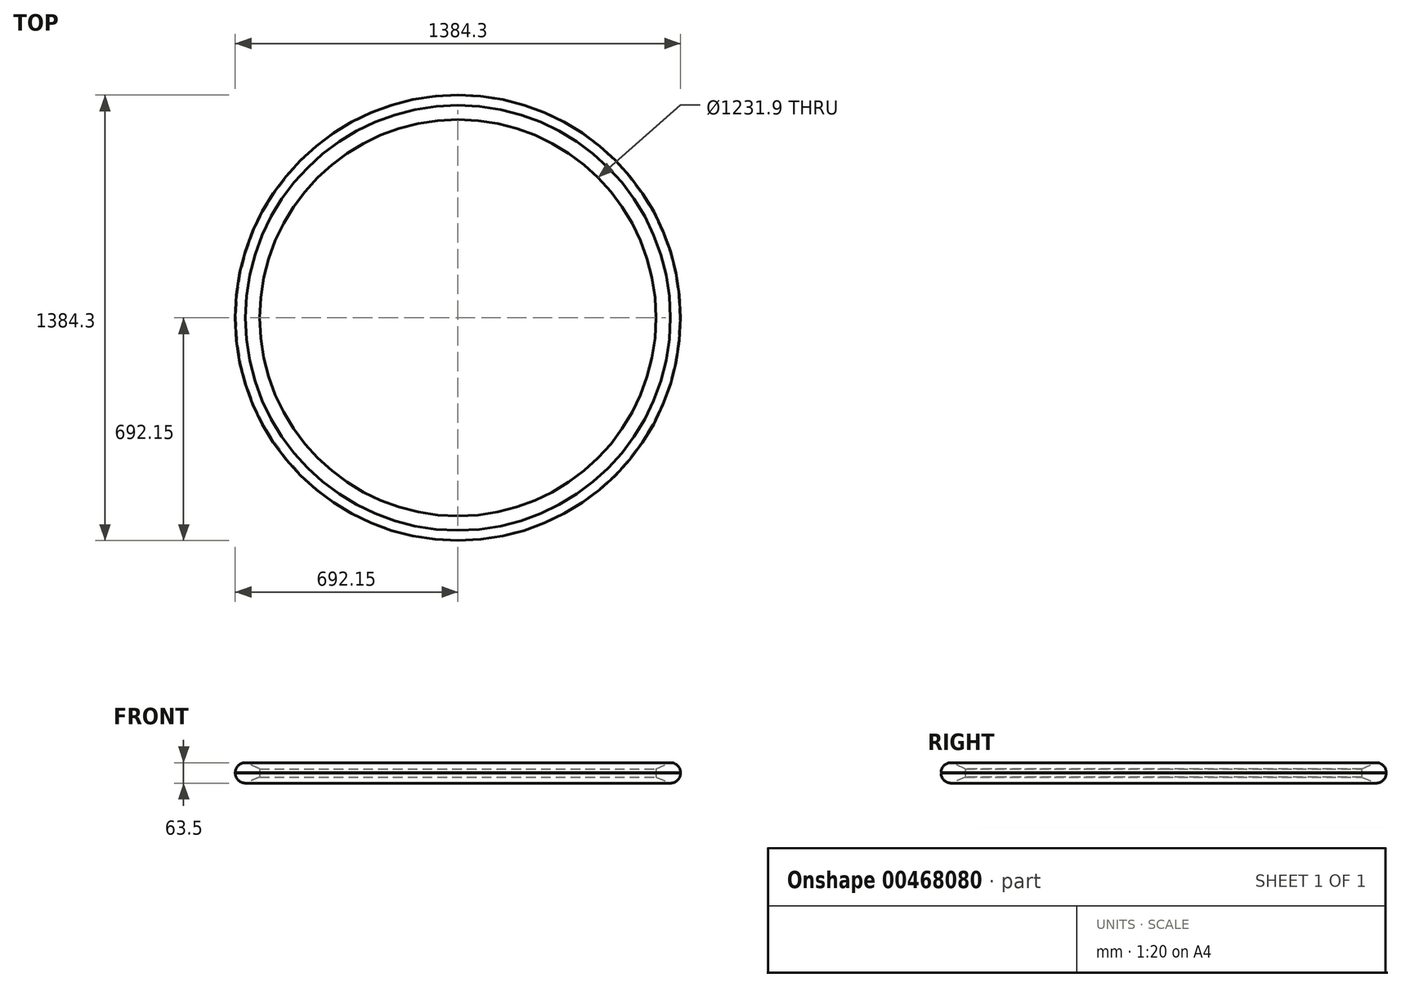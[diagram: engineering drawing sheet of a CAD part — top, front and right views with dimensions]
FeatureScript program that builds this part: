
annotation { "Feature Type Name" : "Feature", "Feature Type Description" : "" }
export const myFeature = defineFeature(function(context is Context, id is Id, definition is map)
    precondition{}
    {
        {
            var Q0;
            Q0=qCreatedBy(makeId("Front.planeOp"),FACE);
            var sketch = newSketch(context, id + "F0", { "sketchPlane" : qUnion([Q0])});
            skLineSegment(sketch, "E0", {"start": v(0, 0) * mm, "end": v(660.4, 0) * mm});
            skLineSegment(sketch, "E1", {"start": v(660.4, 0) * mm, "end": v(615.95, 0) * mm});
            skLineSegment(sketch, "E2", {"start": v(615.95, 0) * mm, "end": v(615.95, 12.7) * mm});
            skLineSegment(sketch, "E3", {"start": v(615.95, 0) * mm, "end": v(615.95, -12.7) * mm});
            skLineSegment(sketch, "E4", {"start": v(0, 0) * mm, "end": v(0, 83.21) * mm});
            skCircle(sketch, "E5", {"center": v(660.4, 0) * mm, "radius": 31.75 * mm});
            skLineSegment(sketch, "E6", {"start": v(615.95, -12.7) * mm, "end": v(660.4, -31.75) * mm});
            skLineSegment(sketch, "E7", {"start": v(615.95, 12.7) * mm, "end": v(660.4, 31.75) * mm});
            skLineSegment(sketch, "E8", {"start": v(692.15, 0) * mm, "end": v(689.6, 0) * mm});
            skLineSegment(sketch, "E9", {"start": v(689.6, 0) * mm, "end": v(689.6, 0.25) * mm});
            skLineSegment(sketch, "E10", {"start": v(689.6, 0.25) * mm, "end": v(692.15, 0.25) * mm});
            skLineSegment(sketch, "E11", {"start": v(689.6, 0) * mm, "end": v(689.6, -0.25) * mm});
            skLineSegment(sketch, "E12", {"start": v(689.6, -0.25) * mm, "end": v(692.15, -0.25) * mm});
            skSolve(sketch);
        }
        {
            var Q0;
            {var subQ0=sQuery(id+"F0.wireOp",EDGE,"BpbeHqKv-90v2-CecC-KdAu-xhUZU532047C");var subQ1=sQuery(id+"F0.wireOp",EDGE,"ouEWdRrN-fbvK-T4IV-dJUb-a4UaIsFi8zsm");var subQ2=makeQuery(id+"F0.imprint","INTERSECT",VERTEX,{"disambiguationData":[OD(0.0)],"derivedFrom":[subQ1,subQ0]});Q0=makeQuery(id+"F0.imprint","IMPRINT",FACE,{"disambiguationData":[TD([[makeQuery(id+"F0.imprint","IMPRINT",EDGE,{"disambiguationData":[TD([[subQ2,-1.0]])],"derivedFrom":subQ1}),1.0]])]});}
            var Q1;
            {var subQ0=sQuery(id+"F0.wireOp",EDGE,"BpbeHqKv-90v2-CecC-KdAu-xhUZU532047C");var subQ1=sQuery(id+"F0.wireOp",EDGE,"ouEWdRrN-fbvK-T4IV-dJUb-a4UaIsFi8zsm");var subQ3=makeQuery(id+"F0.imprint","INTERSECT",VERTEX,{"disambiguationData":[OD(1.0)],"derivedFrom":[subQ1,subQ0]});Q1=makeQuery(id+"F0.imprint","IMPRINT",FACE,{"disambiguationData":[TD([[makeQuery(id+"F0.imprint","IMPRINT",EDGE,{"disambiguationData":[TD([[subQ3,-1.0]])],"derivedFrom":subQ1}),1.0]])]});}
            var Q2;
            {var subQ0=sQuery(id+"F0.wireOp",EDGE,"VjwYH7CL-qhdJ-UY1F-Rfc4-S9BnykVlBEnN");var subQ1=sQuery(id+"F0.wireOp",EDGE,"ouEWdRrN-fbvK-T4IV-dJUb-a4UaIsFi8zsm");var subQ2=makeQuery(id+"F0.imprint","INTERSECT",VERTEX,{"disambiguationData":[OD(0.0)],"derivedFrom":[subQ1,subQ0]});Q2=makeQuery(id+"F0.imprint","IMPRINT",FACE,{"disambiguationData":[TD([[makeQuery(id+"F0.imprint","IMPRINT",EDGE,{"disambiguationData":[TD([[subQ2,1.0]])],"derivedFrom":subQ1}),1.0]])]});}
            var Q3;
            {var subQ5=sQuery(id+"F0.wireOp",EDGE,"E3");Q3=makeQuery(id+"F0.imprint","IMPRINT",FACE,{"disambiguationData":[TD([[makeQuery(id+"F0.imprint","IMPRINT",EDGE,{"derivedFrom":subQ5}),1.0]])]});}
            var Q4;
            {var subQ5=sQuery(id+"F0.wireOp",EDGE,"E2");Q4=makeQuery(id+"F0.imprint","IMPRINT",FACE,{"disambiguationData":[TD([[makeQuery(id+"F0.imprint","IMPRINT",EDGE,{"derivedFrom":subQ5}),-1.0]])]});}
            var Q5;
            {var subQ1=sQuery(id+"F0.wireOp",EDGE,"E5");var subQ5=makeQuery(id+"F0.imprint","INTERSECT",VERTEX,{"derivedFrom":[sQuery(id+"F0.wireOp",EDGE,"E1"),subQ1]});Q5=makeQuery(id+"F0.imprint","IMPRINT",FACE,{"disambiguationData":[TD([[makeQuery(id+"F0.imprint","IMPRINT",EDGE,{"disambiguationData":[TD([[subQ5,1.0]])],"derivedFrom":subQ1}),1.0]])]});}
            var Q6;
            {var subQ0=sQuery(id+"F0.wireOp",EDGE,"E7");var subQ1=sQuery(id+"F0.wireOp",EDGE,"E5");var subQ2=makeQuery(id+"F0.imprint","INTERSECT",VERTEX,{"disambiguationData":[OD(0.0)],"derivedFrom":[subQ1,subQ0]});Q6=makeQuery(id+"F0.imprint","IMPRINT",FACE,{"disambiguationData":[TD([[makeQuery(id+"F0.imprint","IMPRINT",EDGE,{"disambiguationData":[TD([[subQ2,-1.0]])],"derivedFrom":subQ1}),1.0]])]});}
            var Q7;
            {var subQ0=sQuery(id+"F0.wireOp",EDGE,"E6");var subQ1=sQuery(id+"F0.wireOp",EDGE,"E5");var subQ2=makeQuery(id+"F0.imprint","INTERSECT",VERTEX,{"disambiguationData":[OD(0.0)],"derivedFrom":[subQ1,subQ0]});Q7=makeQuery(id+"F0.imprint","IMPRINT",FACE,{"disambiguationData":[TD([[makeQuery(id+"F0.imprint","IMPRINT",EDGE,{"disambiguationData":[TD([[subQ2,1.0]])],"derivedFrom":subQ1}),1.0]])]});}
            var Q8;
            Q8=sQuery(id+"F0.wireOp",EDGE,"E4");
            revolve(context, id + "F1", {"entities" : qUnion([Q0, Q1, Q2, Q3, Q4, Q5, Q6, Q7]), "axis" : qUnion([Q8]), "revolveType" : RevolveType.FULL});
        }
    });
